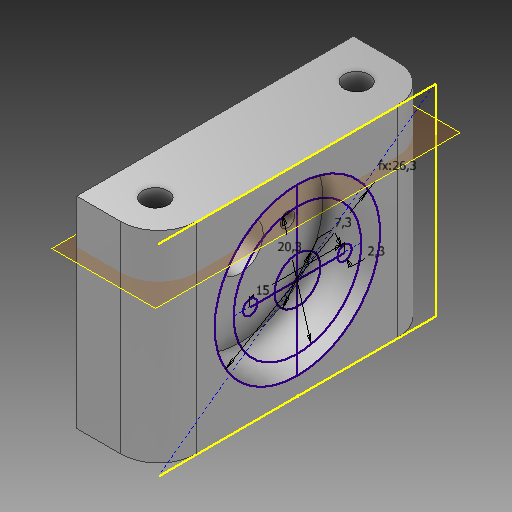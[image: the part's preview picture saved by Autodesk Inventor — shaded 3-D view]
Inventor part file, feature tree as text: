
AUTODESK INVENTOR PART (.ipt)
format: ipt  version: 2020 (Build 240168000, 168)  size: 210,432 bytes
history: native  units: mm
features: extrude x4, sketch x3, other x2, fillet x1, chamfer x1
ambient origin geometry x8: Origin, YZ Plane, XZ Plane, XY Plane, X Axis, Y Axis, Z Axis, Center Point
bodies: Body1 (feature_tree)
feature tree (11):
  other  "Твердое тело1"
  extrude  "Выдавливание1"  Depth=13.0mm
  sketch  "Эскиз2"
  extrude  "Выдавливание3"  Depth=44.0mm
  extrude  "Выдавливание4"  Depth=16.0mm
  other  "РабПлоскость1"
  extrude  "Выдавливание5"  Depth=4.0mm
  fillet  "Сопряжение1"  [1 undecoded]
  chamfer  "Фаска1"  Distance=20.3mm
  sketch  "Эскиз1"
  sketch  "Эскиз3"
note: 1 required parameter value undecoded (feature->parameter linkage not recoverable at this tier; creation-order binding heuristic only, values carry confidence <= 0.55)
